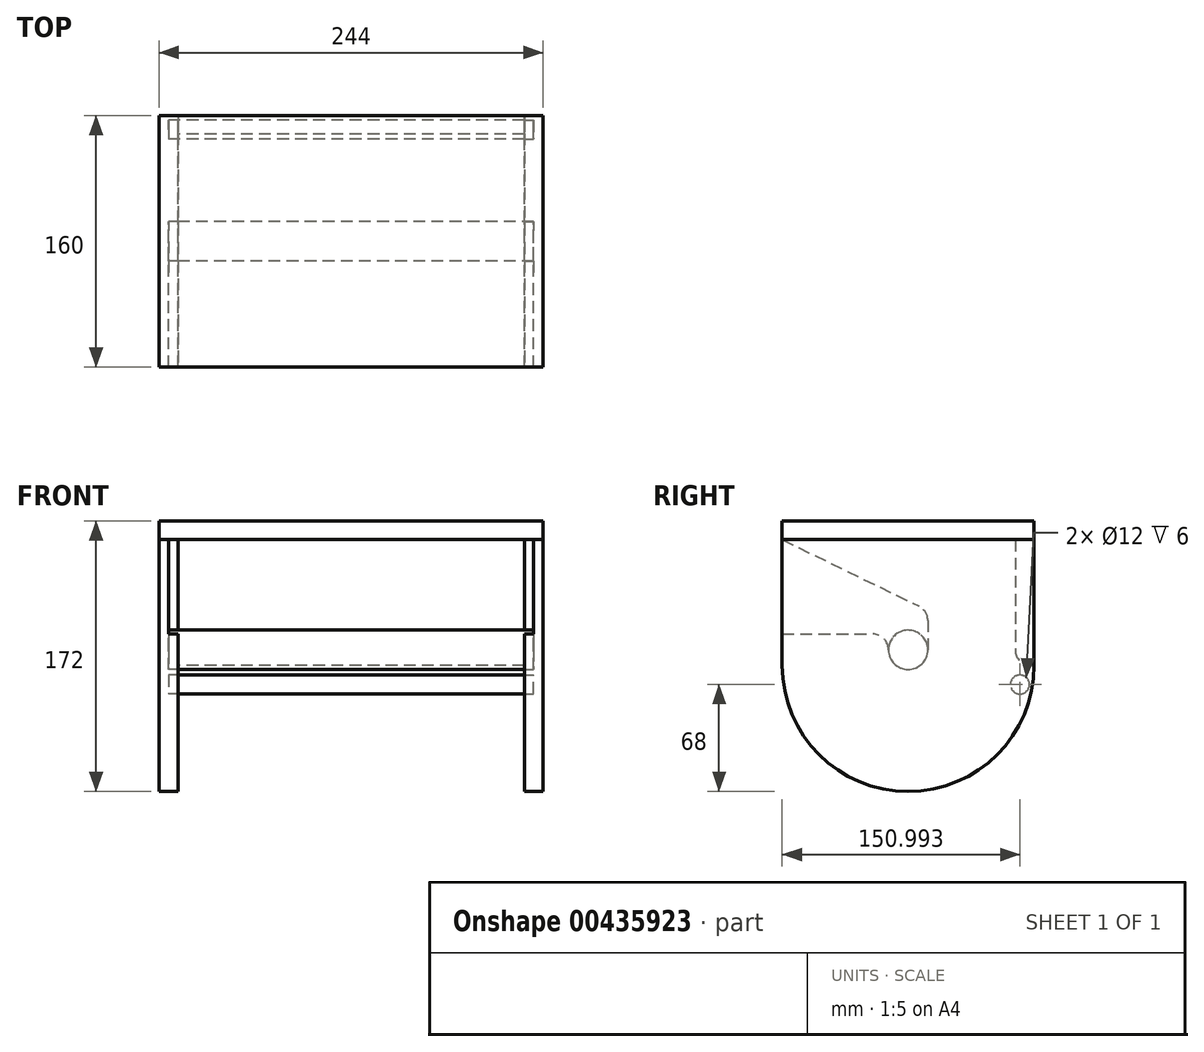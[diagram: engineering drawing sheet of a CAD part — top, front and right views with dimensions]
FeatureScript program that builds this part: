
annotation { "Feature Type Name" : "Feature", "Feature Type Description" : "" }
export const myFeature = defineFeature(function(context is Context, id is Id, definition is map)
    precondition{}
    {
        {
            assignVariable(context, id + "F0", {"name" : "thickness", "anyValue" : 12});
        }
        {
            assignVariable(context, id + "F1", {"name" : "width", "anyValue" : 244});
        }
        {
            var Q0;
            Q0=qCreatedBy(makeId("Right.planeOp"),FACE);
            var sketch = newSketch(context, id + "F2", { "sketchPlane" : qUnion([Q0])});
            skPoint(sketch, "E0.middle", {"position": v(0, 0) * mm});
            skCircle(sketch, "E1", {"center": v(0, 0) * mm, "radius": 80 * mm});
            skCircle(sketch, "E2", {"center": v(0, 0) * mm, "radius": 22.5 * mm, "construction": true});
            skCircle(sketch, "E3", {"center": v(0, 0) * mm, "radius": 50 * mm, "construction": true});
            skCircle(sketch, "E4", {"center": v(0, 10) * mm, "radius": 12.5 * mm});
            skCircle(sketch, "E5", {"center": v(71, -12) * mm, "radius": 6 * mm});
            skLineSegment(sketch, "E6.left", {"start": v(-80, 0) * mm, "end": v(-80, 92) * mm});
            skLineSegment(sketch, "E7", {"start": v(80, 0) * mm, "end": v(80, 92) * mm});
            skLineSegment(sketch, "E8", {"start": v(80, 92) * mm, "end": v(-80, 92) * mm});
            skLineSegment(sketch, "E9", {"start": v(80, 0) * mm, "end": v(78, 0) * mm});
            skLineSegment(sketch, "E10", {"start": v(68, 10) * mm, "end": v(68, 80) * mm});
            skLineSegment(sketch, "E11", {"start": v(80, 80) * mm, "end": v(-80, 80) * mm});
            skPoint(sketch, "E12", {"position": v(-80, 20) * mm});
            skLineSegment(sketch, "E13", {"start": v(12.5, 28.74) * mm, "end": v(12.5, 10) * mm});
            skLineSegment(sketch, "E14", {"start": v(-80, 80) * mm, "end": v(6.87, 37.74) * mm});
            skLineSegment(sketch, "E15", {"start": v(-80, 20) * mm, "end": v(-22.5, 20) * mm});
            skPoint(sketch, "E16.visualSharp", {"position": v(-13.48, 20) * mm});
            skArc(sketch, "E16.filletArc", {"start": v(-12.5, 10) * mm, "mid": v(-15.43, 17.07) * mm, "end": v(-22.5, 20) * mm});
            skPoint(sketch, "E17.visualSharp", {"position": v(12.5, 35) * mm});
            skArc(sketch, "E17.filletArc", {"start": v(12.5, 28.74) * mm, "mid": v(10.98, 34.05) * mm, "end": v(6.87, 37.74) * mm});
            skPoint(sketch, "E18.visualSharp", {"position": v(68, 0) * mm});
            skArc(sketch, "E18.filletArc", {"start": v(68, 10) * mm, "mid": v(70.93, 2.93) * mm, "end": v(78, 0) * mm});
            skSolve(sketch);
        }
        {
            var Q0;
            {var subQ0=sQuery(id+"F2.wireOp",EDGE,"E11");var subQ1=sQuery(id+"F2.wireOp",EDGE,"E1");var subQ2=makeQuery(id+"F2.imprint","INTERSECT",VERTEX,{"derivedFrom":[subQ1,subQ0]});Q0=makeQuery(id+"F2.imprint","IMPRINT",FACE,{"disambiguationData":[TD([[makeQuery(id+"F2.imprint","IMPRINT",EDGE,{"disambiguationData":[TD([[subQ2,-1.0]])],"derivedFrom":subQ1}),-1.0]])]});}
            var Q1;
            Q1=makeQuery(id+"F2.imprint","IMPRINT",FACE,{"disambiguationData":[TD([[makeQuery(id+"F2.imprint","IMPRINT",EDGE,{"derivedFrom":sQuery(id+"F2.wireOp",EDGE,"E5")}),-1.0]])]});
            var Q2;
            {var subQ0=sQuery(id+"F2.wireOp",EDGE,"E10");var subQ1=sQuery(id+"F2.wireOp",EDGE,"E1");var subQ2=makeQuery(id+"F2.imprint","INTERSECT",VERTEX,{"derivedFrom":[subQ1,subQ0]});Q2=makeQuery(id+"F2.imprint","IMPRINT",FACE,{"disambiguationData":[TD([[makeQuery(id+"F2.imprint","IMPRINT",EDGE,{"disambiguationData":[TD([[subQ2,-1.0]])],"derivedFrom":subQ1}),-1.0]])]});}
            var Q3;
            {var subQ0=sQuery(id+"F2.wireOp",EDGE,"E6.left");var subQ1=sQuery(id+"F2.wireOp",EDGE,"E1");var subQ2=makeQuery(id+"F2.imprint","INTERSECT",VERTEX,{"derivedFrom":[subQ1,subQ0]});Q3=makeQuery(id+"F2.imprint","IMPRINT",FACE,{"disambiguationData":[TD([[makeQuery(id+"F2.imprint","IMPRINT",EDGE,{"disambiguationData":[TD([[subQ2,1.0]])],"derivedFrom":subQ1}),-1.0]])]});}
            var Q4;
            {var subQ0=sQuery(id+"F2.wireOp",EDGE,"E9");Q4=makeQuery(id+"F2.imprint","IMPRINT",FACE,{"disambiguationData":[TD([[makeQuery(id+"F2.imprint","IMPRINT",EDGE,{"derivedFrom":subQ0}),-1.0]])]});}
            var Q5;
            {var subQ3=sQuery(id+"F2.wireOp",EDGE,"E10");var subQ5=sQuery(id+"F2.wireOp",EDGE,"E11");var subQ7=makeQuery(id+"F2.imprint","INTERSECT",VERTEX,{"derivedFrom":[subQ3,subQ5]});Q5=makeQuery(id+"F2.imprint","IMPRINT",FACE,{"disambiguationData":[TD([[makeQuery(id+"F2.imprint","IMPRINT",EDGE,{"disambiguationData":[TD([[subQ7,1.0]])],"derivedFrom":subQ3}),-1.0]])]});}
            extrude(context, id + "F3", {"entities" : qUnion([Q0, Q1, Q2, Q3, Q4, Q5]), "depth" : (getVariable(context, 'thickness')) * mm});
        }
        {
            var Q0;
            Q0=makeQuery(id+"F2.imprint","IMPRINT",FACE,{"disambiguationData":[TD([[makeQuery(id+"F2.imprint","IMPRINT",EDGE,{"derivedFrom":sQuery(id+"F2.wireOp",EDGE,"E5")}),1.0]])]});
            var Q1;
            {var subQ0=sQuery(id+"F2.wireOp",EDGE,"E4");var subQ1=makeQuery(id+"F2.imprint","INTERSECT",VERTEX,{"derivedFrom":[subQ0,sQuery(id+"F2.wireOp",EDGE,"E13")]});Q1=makeQuery(id+"F2.imprint","IMPRINT",FACE,{"disambiguationData":[TD([[makeQuery(id+"F2.imprint","IMPRINT",EDGE,{"disambiguationData":[TD([[subQ1,-1.0]])],"derivedFrom":subQ0}),1.0]])]});}
            var Q2;
            {var subQ4=sQuery(id+"F2.wireOp",EDGE,"E13");Q2=makeQuery(id+"F2.imprint","IMPRINT",FACE,{"disambiguationData":[TD([[makeQuery(id+"F2.imprint","IMPRINT",EDGE,{"derivedFrom":subQ4}),-1.0]])]});}
            var Q3;
            {var subQ0=sQuery(id+"F2.wireOp",EDGE,"E14");var subQ1=sQuery(id+"F2.wireOp",EDGE,"E1");var subQ2=makeQuery(id+"F2.imprint","INTERSECT",VERTEX,{"derivedFrom":[subQ1,subQ0]});Q3=makeQuery(id+"F2.imprint","IMPRINT",FACE,{"disambiguationData":[TD([[makeQuery(id+"F2.imprint","IMPRINT",EDGE,{"disambiguationData":[TD([[subQ2,-1.0]])],"derivedFrom":subQ1}),-1.0]])]});}
            extrude(context, id + "F4", {"entities" : qUnion([Q0, Q1, Q2, Q3]), "operationType" : NewBodyOperationType.ADD, "depth" : (getVariable(context, 'thickness') / 2) * mm});
        }
        {
            var Q0;
            {var subQ1=sQuery(id+"F2.wireOp",EDGE,"E8");var subQ6=sQuery(id+"F2.wireOp",EDGE,"E6.left");var subQ7=makeQuery(id+"F2.imprint","INTERSECT",VERTEX,{"derivedFrom":[subQ6,subQ1]});Q0=makeQuery(id+"F2.imprint","IMPRINT",FACE,{"disambiguationData":[TD([[makeQuery(id+"F2.imprint","IMPRINT",EDGE,{"disambiguationData":[TD([[subQ7,1.0]])],"derivedFrom":subQ1}),1.0]])]});}
            extrude(context, id + "F5", {"entities" : qUnion([Q0]), "depth" : (getVariable(context, 'width')) * mm});
        }
        {
            var Q0;
            {var subQ0=sQuery(id+"F2.wireOp",EDGE,"E1");var subQ12=makeQuery(id+"F2.imprint","INTERSECT",VERTEX,{"derivedFrom":[subQ0,sQuery(id+"F2.wireOp",EDGE,"E7")]});Q0=makeQuery(id+"F2.imprint","IMPRINT",FACE,{"disambiguationData":[TD([[makeQuery(id+"F2.imprint","IMPRINT",EDGE,{"disambiguationData":[TD([[subQ12,-1.0]])],"derivedFrom":subQ0}),1.0]])]});}
            cPlane(context, id + "F6", {"entities" : qUnion([Q0]), "cplaneType" : CPlaneType.OFFSET, "offset" : (getVariable(context, 'width') / 2) * mm, "width" : 150 * mm, "height" : 150 * mm});
        }
        {
            var Q0;
            Q0=makeQuery(id+"F3.opExtrude","SWEPT_BODY",BODY,{"disambiguationData":[OSD([sQuery(id+"F2.wireOp",EDGE,"E1"),sQuery(id+"F2.wireOp",EDGE,"E4"),sQuery(id+"F2.wireOp",EDGE,"E5"),sQuery(id+"F2.wireOp",EDGE,"E6.bottom"),sQuery(id+"F2.wireOp",EDGE,"E6.left"),sQuery(id+"F2.wireOp",EDGE,"E7"),sQuery(id+"F2.wireOp",EDGE,"1f991beb-c958-47d1-a605-ca1ea1be66dc"),sQuery(id+"F2.wireOp",EDGE,"7IT19mt9-Ptb6-w6co-XGCE-3NGXy2vIkI0t"),sQuery(id+"F2.wireOp",EDGE,"EBuoTcst-HYsx-fInZ-yGNc-Qp2EeeEodv8E"),sQuery(id+"F2.wireOp",EDGE,"g64pjk3F-r82Y-xJYv-FtWr-zupMu5U47jWR"),sQuery(id+"F2.wireOp",EDGE,"wwz3YBsq-swk9-61A6-9uqQ-SGWFUsr60FiT"),sQuery(id+"F2.wireOp",EDGE,"djkX6LHT-dnZk-TJcp-iquZ-90cpqfovkZvz")])]});
            var Q1;
            Q1=qCreatedBy(id+"F6.planeOp",FACE);
            mirror(context, id + "F7", {"entities" : qUnion([Q0]), "mirrorPlane" : qUnion([Q1])});
        }
        {
            var Q0;
            Q0=makeQuery(id+"F4.opExtrude","CAP_FACE",FACE,{"disambiguationData":[OSD([sQuery(id+"F2.wireOp",EDGE,"E5")])],"isStart":false});
            var Q1;
            Q1=sQuery(id+"F2.wireOp",EDGE,"E5");
            var Q2;
            Q2=makeQuery(id+"F7.opPattern","COPY",FACE,{"derivedFrom":makeQuery(id+"F3.opExtrude","CAP_FACE",FACE,{"disambiguationData":[OSD([sQuery(id+"F2.wireOp",EDGE,"E1"),sQuery(id+"F2.wireOp",EDGE,"E4"),sQuery(id+"F2.wireOp",EDGE,"E5"),sQuery(id+"F2.wireOp",EDGE,"E6.left"),sQuery(id+"F2.wireOp",EDGE,"E10"),sQuery(id+"F2.wireOp",EDGE,"E11"),sQuery(id+"F2.wireOp",EDGE,"E13"),sQuery(id+"F2.wireOp",EDGE,"5366b9c5-c7fe-4c7c-b21e-67f2f189e9f0"),sQuery(id+"F2.wireOp",EDGE,"E14"),sQuery(id+"F2.wireOp",EDGE,"E15"),sQuery(id+"F2.wireOp",EDGE,"yAHrhf6Q-7W7J-1P8k-Nwhg-wUorw8kZrY0l"),sQuery(id+"F2.wireOp",EDGE,"E16.filletArc"),sQuery(id+"F2.wireOp",EDGE,"E17.filletArc")])],"isStart":false}),"instanceName":"1"});
            extrude(context, id + "F8", {"entities" : qUnion([Q0]), "surfaceEntities" : qUnion([Q1]), "endBound" : BoundingType.UP_TO_SURFACE, "endBoundEntityFace" : qUnion([Q2]), "depth" : 25 * mm});
        }
        {
            var Q0;
            {var subQ0=sQuery(id+"F2.wireOp",EDGE,"E4");var subQ1=makeQuery(id+"F2.imprint","INTERSECT",VERTEX,{"derivedFrom":[subQ0,sQuery(id+"F2.wireOp",EDGE,"7IT19mt9-Ptb6-w6co-XGCE-3NGXy2vIkI0t")]});Q0=makeQuery(id+"F2.imprint","IMPRINT",FACE,{"disambiguationData":[TD([[makeQuery(id+"F2.imprint","IMPRINT",EDGE,{"disambiguationData":[TD([[subQ1,1.0]])],"derivedFrom":subQ0}),1.0]])]});}
            var Q1;
            Q1=sQuery(id+"F2.wireOp",EDGE,"E4");
            var Q2;
            Q2=makeQuery(id+"F7.opPattern","COPY",FACE,{"derivedFrom":makeQuery(id+"F4.opExtrude","CAP_FACE",FACE,{"disambiguationData":[OSD([sQuery(id+"F2.wireOp",EDGE,"E4"),sQuery(id+"F2.wireOp",EDGE,"E7"),sQuery(id+"F2.wireOp",EDGE,"1f991beb-c958-47d1-a605-ca1ea1be66dc"),sQuery(id+"F2.wireOp",EDGE,"7IT19mt9-Ptb6-w6co-XGCE-3NGXy2vIkI0t"),sQuery(id+"F2.wireOp",EDGE,"EBuoTcst-HYsx-fInZ-yGNc-Qp2EeeEodv8E")])],"isStart":false}),"instanceName":"1"});
            var Q3;
            Q3=makeQuery(id+"F4.opExtrude","CAP_FACE",FACE,{"disambiguationData":[OSD([sQuery(id+"F2.wireOp",EDGE,"E4"),sQuery(id+"F2.wireOp",EDGE,"E7"),sQuery(id+"F2.wireOp",EDGE,"1f991beb-c958-47d1-a605-ca1ea1be66dc"),sQuery(id+"F2.wireOp",EDGE,"7IT19mt9-Ptb6-w6co-XGCE-3NGXy2vIkI0t"),sQuery(id+"F2.wireOp",EDGE,"EBuoTcst-HYsx-fInZ-yGNc-Qp2EeeEodv8E")])],"isStart":false});
            extrude(context, id + "F9", {"entities" : qUnion([Q0]), "surfaceEntities" : qUnion([Q1]), "endBound" : BoundingType.UP_TO_SURFACE, "endBoundEntityFace" : qUnion([Q2]), "depth" : 25 * mm, "hasSecondDirection" : true, "secondDirectionBound" : SecondDirectionBoundingType.UP_TO_SURFACE, "secondDirectionOppositeDirection" : false, "secondDirectionBoundEntityFace" : qUnion([Q3]), "secondDirectionDepth" : -6 * mm});
        }
        {
            var Q0;
            {var subQ1=sQuery(id+"F2.wireOp",EDGE,"E7");Q0=makeQuery(id+"F2.imprint","IMPRINT",FACE,{"disambiguationData":[TD([[makeQuery(id+"F2.imprint","IMPRINT",EDGE,{"derivedFrom":subQ1}),1.0]])]});}
            var Q1;
            {var subQ0=sQuery(id+"F2.wireOp",EDGE,"E9");Q1=makeQuery(id+"F2.imprint","IMPRINT",FACE,{"disambiguationData":[TD([[makeQuery(id+"F2.imprint","IMPRINT",EDGE,{"derivedFrom":subQ0}),-1.0]])]});}
            var Q2;
            Q2=makeQuery(id+"F7.opPattern","COPY",FACE,{"derivedFrom":makeQuery(id+"F3.opExtrude","CAP_FACE",FACE,{"disambiguationData":[OSD([sQuery(id+"F2.wireOp",EDGE,"E1"),sQuery(id+"F2.wireOp",EDGE,"E4"),sQuery(id+"F2.wireOp",EDGE,"E5"),sQuery(id+"F2.wireOp",EDGE,"E6.left"),sQuery(id+"F2.wireOp",EDGE,"E7"),sQuery(id+"F2.wireOp",EDGE,"E11"),sQuery(id+"F2.wireOp",EDGE,"E13"),sQuery(id+"F2.wireOp",EDGE,"E14"),sQuery(id+"F2.wireOp",EDGE,"E15"),sQuery(id+"F2.wireOp",EDGE,"E16.filletArc"),sQuery(id+"F2.wireOp",EDGE,"E17.filletArc")])],"isStart":false}),"instanceName":"1"});
            var Q3;
            Q3=makeQuery(id+"F3.opExtrude","CAP_FACE",FACE,{"disambiguationData":[OSD([sQuery(id+"F2.wireOp",EDGE,"E1"),sQuery(id+"F2.wireOp",EDGE,"E4"),sQuery(id+"F2.wireOp",EDGE,"E5"),sQuery(id+"F2.wireOp",EDGE,"E6.left"),sQuery(id+"F2.wireOp",EDGE,"E7"),sQuery(id+"F2.wireOp",EDGE,"E11"),sQuery(id+"F2.wireOp",EDGE,"E13"),sQuery(id+"F2.wireOp",EDGE,"E14"),sQuery(id+"F2.wireOp",EDGE,"E15"),sQuery(id+"F2.wireOp",EDGE,"E16.filletArc"),sQuery(id+"F2.wireOp",EDGE,"E17.filletArc")])],"isStart":false});
            extrude(context, id + "F10", {"entities" : qUnion([Q0, Q1]), "endBound" : BoundingType.UP_TO_SURFACE, "endBoundEntityFace" : qUnion([Q2]), "depth" : 25 * mm, "hasSecondDirection" : true, "secondDirectionBound" : SecondDirectionBoundingType.UP_TO_SURFACE, "secondDirectionOppositeDirection" : false, "secondDirectionBoundEntityFace" : qUnion([Q3]), "secondDirectionDepth" : 25 * mm});
        }
    });
